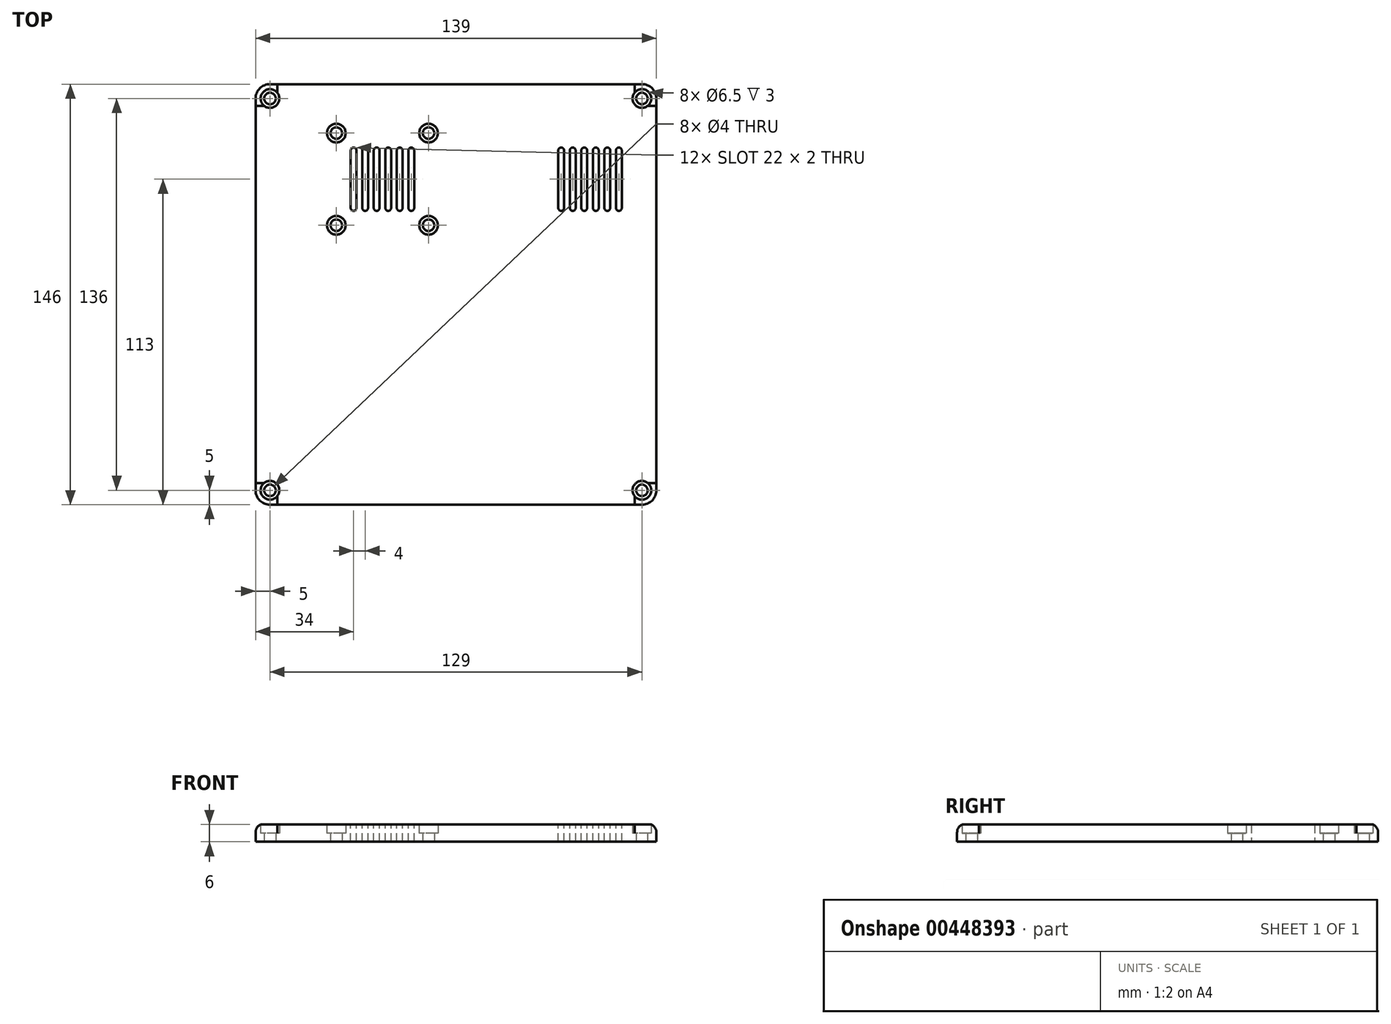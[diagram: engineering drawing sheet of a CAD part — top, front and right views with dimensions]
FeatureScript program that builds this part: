
annotation { "Feature Type Name" : "Feature", "Feature Type Description" : "" }
export const myFeature = defineFeature(function(context is Context, id is Id, definition is map)
    precondition{}
    {
        {
            var Q0;
            Q0=qCreatedBy(makeId("Top.planeOp"),FACE);
            var sketch = newSketch(context, id + "F0", { "sketchPlane" : qUnion([Q0])});
            skLineSegment(sketch, "E0.bottom", {"start": v(63.5, -70) * mm, "end": v(-63.5, -70) * mm});
            skLineSegment(sketch, "E0.top", {"start": v(63.5, 70) * mm, "end": v(-63.5, 70) * mm});
            skLineSegment(sketch, "E0.left", {"start": v(66.5, -67) * mm, "end": v(66.5, 67) * mm});
            skLineSegment(sketch, "E0.right", {"start": v(-66.5, -67) * mm, "end": v(-66.5, 67) * mm});
            skPoint(sketch, "E0.middle", {"position": v(0, 0) * mm});
            skLineSegment(sketch, "E1.bottom", {"start": v(64.5, -73) * mm, "end": v(-64.5, -73) * mm});
            skLineSegment(sketch, "E1.top", {"start": v(64.5, 73) * mm, "end": v(-64.5, 73) * mm});
            skLineSegment(sketch, "E1.left", {"start": v(69.5, -68) * mm, "end": v(69.5, 68) * mm});
            skLineSegment(sketch, "E1.right", {"start": v(-69.5, -68) * mm, "end": v(-69.5, 68) * mm});
            skPoint(sketch, "E2.visualSharp", {"position": v(-69.5, 73) * mm});
            skArc(sketch, "E2.filletArc", {"start": v(-64.5, 73) * mm, "mid": v(-68.04, 71.54) * mm, "end": v(-69.5, 68) * mm});
            skPoint(sketch, "E3.visualSharp", {"position": v(69.5, 73) * mm});
            skArc(sketch, "E3.filletArc", {"start": v(69.5, 68) * mm, "mid": v(68.04, 71.54) * mm, "end": v(64.5, 73) * mm});
            skPoint(sketch, "E4.visualSharp", {"position": v(-69.5, -73) * mm});
            skArc(sketch, "E4.filletArc", {"start": v(-69.5, -68) * mm, "mid": v(-68.04, -71.54) * mm, "end": v(-64.5, -73) * mm});
            skPoint(sketch, "E5.visualSharp", {"position": v(69.5, -73) * mm});
            skArc(sketch, "E5.filletArc", {"start": v(64.5, -73) * mm, "mid": v(68.04, -71.54) * mm, "end": v(69.5, -68) * mm});
            skPoint(sketch, "E6.visualSharp", {"position": v(66.5, 70) * mm});
            skArc(sketch, "E6.filletArc", {"start": v(66.5, 67) * mm, "mid": v(65.62, 69.12) * mm, "end": v(63.5, 70) * mm});
            skPoint(sketch, "E7.visualSharp", {"position": v(-66.5, 70) * mm});
            skArc(sketch, "E7.filletArc", {"start": v(-63.5, 70) * mm, "mid": v(-65.62, 69.12) * mm, "end": v(-66.5, 67) * mm});
            skPoint(sketch, "E8.visualSharp", {"position": v(-66.5, -70) * mm});
            skArc(sketch, "E8.filletArc", {"start": v(-66.5, -67) * mm, "mid": v(-65.62, -69.12) * mm, "end": v(-63.5, -70) * mm});
            skPoint(sketch, "E9.visualSharp", {"position": v(66.5, -70) * mm});
            skArc(sketch, "E9.filletArc", {"start": v(63.5, -70) * mm, "mid": v(65.62, -69.12) * mm, "end": v(66.5, -67) * mm});
            skCircle(sketch, "E10", {"center": v(-64.5, 68) * mm, "radius": 3.25 * mm});
            skCircle(sketch, "E11", {"center": v(-64.5, 68) * mm, "radius": 2 * mm});
            skCircle(sketch, "E12", {"center": v(64.5, 68) * mm, "radius": 3.25 * mm});
            skCircle(sketch, "E13", {"center": v(64.5, 68) * mm, "radius": 2 * mm});
            skCircle(sketch, "E14", {"center": v(64.5, -68) * mm, "radius": 3.25 * mm});
            skCircle(sketch, "E15", {"center": v(64.5, -68) * mm, "radius": 2 * mm});
            skCircle(sketch, "E16", {"center": v(-64.5, -68) * mm, "radius": 3.25 * mm});
            skCircle(sketch, "E17", {"center": v(-64.5, -68) * mm, "radius": 2 * mm});
            skCircle(sketch, "E18", {"center": v(-41.5, 56) * mm, "radius": 3.25 * mm});
            skCircle(sketch, "E19", {"center": v(-9.5, 56) * mm, "radius": 3.25 * mm});
            skCircle(sketch, "E20", {"center": v(-41.5, 24) * mm, "radius": 3.25 * mm});
            skCircle(sketch, "E21", {"center": v(-9.5, 24) * mm, "radius": 3.25 * mm});
            skCircle(sketch, "E22", {"center": v(-9.5, 56) * mm, "radius": 2 * mm});
            skCircle(sketch, "E23", {"center": v(-41.5, 56) * mm, "radius": 2 * mm});
            skCircle(sketch, "E24", {"center": v(-41.5, 24) * mm, "radius": 2 * mm});
            skCircle(sketch, "E25", {"center": v(-9.5, 24) * mm, "radius": 2 * mm});
            skSolve(sketch);
        }
        {
            var Q0;
            {var subQ5=sQuery(id+"F0.wireOp",EDGE,"E14");var subQ10=sQuery(id+"F0.wireOp",EDGE,"E0.bottom");var subQ11=makeQuery(id+"F0.imprint","INTERSECT",VERTEX,{"derivedFrom":[subQ10,subQ5]});Q0=makeQuery(id+"F0.imprint","IMPRINT",FACE,{"disambiguationData":[TD([[makeQuery(id+"F0.imprint","IMPRINT",EDGE,{"disambiguationData":[TD([[subQ11,-1.0]])],"derivedFrom":subQ10}),-1.0]])]});}
            var Q1;
            Q1=makeQuery(id+"F0.imprint","IMPRINT",FACE,{"disambiguationData":[TD([[makeQuery(id+"F0.imprint","IMPRINT",EDGE,{"derivedFrom":sQuery(id+"F0.wireOp",EDGE,"E1.bottom")}),-1.0]])]});
            extrude(context, id + "F1", {"entities" : qUnion([Q0, Q1]), "depth" : 6 * mm});
        }
        {
            var Q0;
            Q0 = qSketchRegion(id + "F0", true);
            var Q1;
            {var subQ0=sQuery(id+"F0.wireOp",EDGE,"E7.filletArc");var subQ1=sQuery(id+"F0.wireOp",EDGE,"E0.top");var subQ2=makeQuery(id+"F0.imprint","INTERSECT",VERTEX,{"derivedFrom":[subQ1,subQ0]});Q1=makeQuery(id+"F0.imprint","IMPRINT",FACE,{"disambiguationData":[TD([[makeQuery(id+"F0.imprint","IMPRINT",EDGE,{"disambiguationData":[TD([[subQ2,1.0]])],"derivedFrom":subQ1}),1.0]])]});}
            var Q2;
            {var subQ0=sQuery(id+"F0.wireOp",EDGE,"E7.filletArc");var subQ1=sQuery(id+"F0.wireOp",EDGE,"E0.top");var subQ2=makeQuery(id+"F0.imprint","INTERSECT",VERTEX,{"derivedFrom":[subQ1,subQ0]});Q2=makeQuery(id+"F0.imprint","IMPRINT",FACE,{"disambiguationData":[TD([[makeQuery(id+"F0.imprint","IMPRINT",EDGE,{"disambiguationData":[TD([[subQ2,1.0]])],"derivedFrom":subQ1}),-1.0]])]});}
            var Q3;
            {var subQ0=sQuery(id+"F0.wireOp",EDGE,"E8.filletArc");var subQ1=sQuery(id+"F0.wireOp",EDGE,"E0.bottom");var subQ2=makeQuery(id+"F0.imprint","INTERSECT",VERTEX,{"derivedFrom":[subQ1,subQ0]});Q3=makeQuery(id+"F0.imprint","IMPRINT",FACE,{"disambiguationData":[TD([[makeQuery(id+"F0.imprint","IMPRINT",EDGE,{"disambiguationData":[TD([[subQ2,1.0]])],"derivedFrom":subQ1}),-1.0]])]});}
            var Q4;
            {var subQ0=sQuery(id+"F0.wireOp",EDGE,"E8.filletArc");var subQ1=sQuery(id+"F0.wireOp",EDGE,"E0.bottom");var subQ2=makeQuery(id+"F0.imprint","INTERSECT",VERTEX,{"derivedFrom":[subQ1,subQ0]});Q4=makeQuery(id+"F0.imprint","IMPRINT",FACE,{"disambiguationData":[TD([[makeQuery(id+"F0.imprint","IMPRINT",EDGE,{"disambiguationData":[TD([[subQ2,1.0]])],"derivedFrom":subQ1}),1.0]])]});}
            var Q5;
            {var subQ0=sQuery(id+"F0.wireOp",EDGE,"E9.filletArc");var subQ1=sQuery(id+"F0.wireOp",EDGE,"E0.bottom");var subQ2=makeQuery(id+"F0.imprint","INTERSECT",VERTEX,{"derivedFrom":[subQ1,subQ0]});Q5=makeQuery(id+"F0.imprint","IMPRINT",FACE,{"disambiguationData":[TD([[makeQuery(id+"F0.imprint","IMPRINT",EDGE,{"disambiguationData":[TD([[subQ2,-1.0]])],"derivedFrom":subQ1}),-1.0]])]});}
            var Q6;
            {var subQ0=sQuery(id+"F0.wireOp",EDGE,"E9.filletArc");var subQ1=sQuery(id+"F0.wireOp",EDGE,"E0.bottom");var subQ2=makeQuery(id+"F0.imprint","INTERSECT",VERTEX,{"derivedFrom":[subQ1,subQ0]});Q6=makeQuery(id+"F0.imprint","IMPRINT",FACE,{"disambiguationData":[TD([[makeQuery(id+"F0.imprint","IMPRINT",EDGE,{"disambiguationData":[TD([[subQ2,-1.0]])],"derivedFrom":subQ1}),1.0]])]});}
            var Q7;
            {var subQ0=sQuery(id+"F0.wireOp",EDGE,"E6.filletArc");var subQ1=sQuery(id+"F0.wireOp",EDGE,"E0.top");var subQ2=makeQuery(id+"F0.imprint","INTERSECT",VERTEX,{"derivedFrom":[subQ1,subQ0]});Q7=makeQuery(id+"F0.imprint","IMPRINT",FACE,{"disambiguationData":[TD([[makeQuery(id+"F0.imprint","IMPRINT",EDGE,{"disambiguationData":[TD([[subQ2,-1.0]])],"derivedFrom":subQ1}),-1.0]])]});}
            var Q8;
            {var subQ0=sQuery(id+"F0.wireOp",EDGE,"E6.filletArc");var subQ1=sQuery(id+"F0.wireOp",EDGE,"E0.top");var subQ2=makeQuery(id+"F0.imprint","INTERSECT",VERTEX,{"derivedFrom":[subQ1,subQ0]});Q8=makeQuery(id+"F0.imprint","IMPRINT",FACE,{"disambiguationData":[TD([[makeQuery(id+"F0.imprint","IMPRINT",EDGE,{"disambiguationData":[TD([[subQ2,-1.0]])],"derivedFrom":subQ1}),1.0]])]});}
            var Q9;
            Q9=makeQuery(id+"F0.imprint","IMPRINT",FACE,{"disambiguationData":[TD([[makeQuery(id+"F0.imprint","IMPRINT",EDGE,{"derivedFrom":sQuery(id+"F0.wireOp",EDGE,"E18")}),1.0]])]});
            var Q10;
            Q10=makeQuery(id+"F0.imprint","IMPRINT",FACE,{"disambiguationData":[TD([[makeQuery(id+"F0.imprint","IMPRINT",EDGE,{"derivedFrom":sQuery(id+"F0.wireOp",EDGE,"E19")}),1.0]])]});
            var Q11;
            Q11=makeQuery(id+"F0.imprint","IMPRINT",FACE,{"disambiguationData":[TD([[makeQuery(id+"F0.imprint","IMPRINT",EDGE,{"derivedFrom":sQuery(id+"F0.wireOp",EDGE,"E20")}),1.0]])]});
            var Q12;
            Q12=makeQuery(id+"F0.imprint","IMPRINT",FACE,{"disambiguationData":[TD([[makeQuery(id+"F0.imprint","IMPRINT",EDGE,{"derivedFrom":sQuery(id+"F0.wireOp",EDGE,"E21")}),1.0]])]});
            extrude(context, id + "F2", {"entities" : qUnion([Q0, Q1, Q2, Q3, Q4, Q5, Q6, Q7, Q8, Q9, Q10, Q11, Q12]), "operationType" : NewBodyOperationType.ADD, "depth" : 3 * mm});
        }
        {
            var Q0;
            Q0=makeQuery(id+"F1.opExtrude","CAP_EDGE",EDGE,{"disambiguationData":[OSD([sQuery(id+"F0.wireOp",EDGE,"E1.bottom")])],"isStart":false});
            fillet(context, id + "F3", {"entities" : qUnion([Q0]), "radius" : 3 * mm, "tangentPropagation" : true, "allowEdgeOverflow" : false});
        }
        {
            var Q0;
            Q0=makeQuery(id+"F1.opExtrude","CAP_FACE",FACE,{"disambiguationData":[OSD([sQuery(id+"F0.wireOp",EDGE,"E1.bottom"),sQuery(id+"F0.wireOp",EDGE,"E1.top"),sQuery(id+"F0.wireOp",EDGE,"E1.left"),sQuery(id+"F0.wireOp",EDGE,"E1.right"),sQuery(id+"F0.wireOp",EDGE,"E2.filletArc"),sQuery(id+"F0.wireOp",EDGE,"E3.filletArc"),sQuery(id+"F0.wireOp",EDGE,"E4.filletArc"),sQuery(id+"F0.wireOp",EDGE,"E5.filletArc"),sQuery(id+"F0.wireOp",EDGE,"E10"),sQuery(id+"F0.wireOp",EDGE,"E12"),sQuery(id+"F0.wireOp",EDGE,"E14"),sQuery(id+"F0.wireOp",EDGE,"E16"),sQuery(id+"F0.wireOp",EDGE,"E18"),sQuery(id+"F0.wireOp",EDGE,"E19"),sQuery(id+"F0.wireOp",EDGE,"E20"),sQuery(id+"F0.wireOp",EDGE,"E21")])],"isStart":false});
            var sketch = newSketch(context, id + "F4", { "sketchPlane" : qUnion([Q0])});
            skLineSegment(sketch, "E26.bottom", {"start": v(-30.5, 29) * mm, "end": v(-32.5, 29) * mm});
            skLineSegment(sketch, "E26.top", {"start": v(-30.5, 51) * mm, "end": v(-32.5, 51) * mm});
            skLineSegment(sketch, "E26.left", {"start": v(-30.5, 29) * mm, "end": v(-30.5, 51) * mm});
            skLineSegment(sketch, "E26.right", {"start": v(-32.5, 29) * mm, "end": v(-32.5, 51) * mm});
            skPoint(sketch, "E26.middle", {"position": v(-31.5, 40) * mm});
            skLineSegment(sketch, "E27.bottom", {"start": v(-26.5, 29) * mm, "end": v(-28.5, 29) * mm});
            skLineSegment(sketch, "E27.top", {"start": v(-26.5, 51) * mm, "end": v(-28.5, 51) * mm});
            skLineSegment(sketch, "E27.left", {"start": v(-26.5, 29) * mm, "end": v(-26.5, 51) * mm});
            skLineSegment(sketch, "E27.right", {"start": v(-28.5, 29) * mm, "end": v(-28.5, 51) * mm});
            skPoint(sketch, "E27.middle", {"position": v(-27.5, 40) * mm});
            skLineSegment(sketch, "E28.bottom", {"start": v(-22.5, 29) * mm, "end": v(-24.5, 29) * mm});
            skLineSegment(sketch, "E28.top", {"start": v(-22.5, 51) * mm, "end": v(-24.5, 51) * mm});
            skLineSegment(sketch, "E28.left", {"start": v(-22.5, 29) * mm, "end": v(-22.5, 51) * mm});
            skLineSegment(sketch, "E28.right", {"start": v(-24.5, 29) * mm, "end": v(-24.5, 51) * mm});
            skPoint(sketch, "E28.middle", {"position": v(-23.5, 40) * mm});
            skLineSegment(sketch, "E29.bottom", {"start": v(-18.5, 29) * mm, "end": v(-20.5, 29) * mm});
            skLineSegment(sketch, "E29.top", {"start": v(-18.5, 51) * mm, "end": v(-20.5, 51) * mm});
            skLineSegment(sketch, "E29.left", {"start": v(-18.5, 29) * mm, "end": v(-18.5, 51) * mm});
            skLineSegment(sketch, "E29.right", {"start": v(-20.5, 29) * mm, "end": v(-20.5, 51) * mm});
            skPoint(sketch, "E29.middle", {"position": v(-19.5, 40) * mm});
            skLineSegment(sketch, "E30.bottom", {"start": v(-14.5, 29) * mm, "end": v(-16.5, 29) * mm});
            skLineSegment(sketch, "E30.top", {"start": v(-14.5, 51) * mm, "end": v(-16.5, 51) * mm});
            skLineSegment(sketch, "E30.left", {"start": v(-14.5, 29) * mm, "end": v(-14.5, 51) * mm});
            skLineSegment(sketch, "E30.right", {"start": v(-16.5, 29) * mm, "end": v(-16.5, 51) * mm});
            skPoint(sketch, "E30.middle", {"position": v(-15.5, 40) * mm});
            skLineSegment(sketch, "E31.bottom", {"start": v(-34.5, 29) * mm, "end": v(-36.5, 29) * mm});
            skLineSegment(sketch, "E31.top", {"start": v(-34.5, 51) * mm, "end": v(-36.5, 51) * mm});
            skLineSegment(sketch, "E31.left", {"start": v(-34.5, 29) * mm, "end": v(-34.5, 51) * mm});
            skLineSegment(sketch, "E31.right", {"start": v(-36.5, 29) * mm, "end": v(-36.5, 51) * mm});
            skPoint(sketch, "E31.middle", {"position": v(-35.5, 40) * mm});
            skLineSegment(sketch, "E32.bottom", {"start": v(41.5, 29) * mm, "end": v(39.5, 29) * mm});
            skLineSegment(sketch, "E32.top", {"start": v(41.5, 51) * mm, "end": v(39.5, 51) * mm});
            skLineSegment(sketch, "E32.left", {"start": v(41.5, 29) * mm, "end": v(41.5, 51) * mm});
            skLineSegment(sketch, "E32.right", {"start": v(39.5, 29) * mm, "end": v(39.5, 51) * mm});
            skPoint(sketch, "E32.middle", {"position": v(40.5, 40) * mm});
            skLineSegment(sketch, "E33.bottom", {"start": v(45.5, 29) * mm, "end": v(43.5, 29) * mm});
            skLineSegment(sketch, "E33.top", {"start": v(45.5, 51) * mm, "end": v(43.5, 51) * mm});
            skLineSegment(sketch, "E33.left", {"start": v(45.5, 29) * mm, "end": v(45.5, 51) * mm});
            skLineSegment(sketch, "E33.right", {"start": v(43.5, 29) * mm, "end": v(43.5, 51) * mm});
            skPoint(sketch, "E33.middle", {"position": v(44.5, 40) * mm});
            skLineSegment(sketch, "E34.bottom", {"start": v(49.5, 29) * mm, "end": v(47.5, 29) * mm});
            skLineSegment(sketch, "E34.top", {"start": v(49.5, 51) * mm, "end": v(47.5, 51) * mm});
            skLineSegment(sketch, "E34.left", {"start": v(49.5, 29) * mm, "end": v(49.5, 51) * mm});
            skLineSegment(sketch, "E34.right", {"start": v(47.5, 29) * mm, "end": v(47.5, 51) * mm});
            skPoint(sketch, "E34.middle", {"position": v(48.5, 40) * mm});
            skLineSegment(sketch, "E35.bottom", {"start": v(53.5, 29) * mm, "end": v(51.5, 29) * mm});
            skLineSegment(sketch, "E35.top", {"start": v(53.5, 51) * mm, "end": v(51.5, 51) * mm});
            skLineSegment(sketch, "E35.left", {"start": v(53.5, 29) * mm, "end": v(53.5, 51) * mm});
            skLineSegment(sketch, "E35.right", {"start": v(51.5, 29) * mm, "end": v(51.5, 51) * mm});
            skPoint(sketch, "E35.middle", {"position": v(52.5, 40) * mm});
            skLineSegment(sketch, "E36.bottom", {"start": v(57.5, 29) * mm, "end": v(55.5, 29) * mm});
            skLineSegment(sketch, "E36.top", {"start": v(57.5, 51) * mm, "end": v(55.5, 51) * mm});
            skLineSegment(sketch, "E36.left", {"start": v(57.5, 29) * mm, "end": v(57.5, 51) * mm});
            skLineSegment(sketch, "E36.right", {"start": v(55.5, 29) * mm, "end": v(55.5, 51) * mm});
            skPoint(sketch, "E36.middle", {"position": v(56.5, 40) * mm});
            skLineSegment(sketch, "E37.bottom", {"start": v(37.5, 29) * mm, "end": v(35.5, 29) * mm});
            skLineSegment(sketch, "E37.top", {"start": v(37.5, 51) * mm, "end": v(35.5, 51) * mm});
            skLineSegment(sketch, "E37.left", {"start": v(37.5, 29) * mm, "end": v(37.5, 51) * mm});
            skLineSegment(sketch, "E37.right", {"start": v(35.5, 29) * mm, "end": v(35.5, 51) * mm});
            skPoint(sketch, "E37.middle", {"position": v(36.5, 40) * mm});
            skSolve(sketch);
        }
        {
            var Q0;
            Q0=makeQuery(id+"F4.imprint","IMPRINT",FACE,{"disambiguationData":[TD([[makeQuery(id+"F4.imprint","IMPRINT",EDGE,{"derivedFrom":sQuery(id+"F4.wireOp",EDGE,"E31.bottom")}),-1.0]])]});
            var Q1;
            Q1=makeQuery(id+"F4.imprint","IMPRINT",FACE,{"disambiguationData":[TD([[makeQuery(id+"F4.imprint","IMPRINT",EDGE,{"derivedFrom":sQuery(id+"F4.wireOp",EDGE,"E26.bottom")}),-1.0]])]});
            var Q2;
            Q2=makeQuery(id+"F4.imprint","IMPRINT",FACE,{"disambiguationData":[TD([[makeQuery(id+"F4.imprint","IMPRINT",EDGE,{"derivedFrom":sQuery(id+"F4.wireOp",EDGE,"E27.bottom")}),-1.0]])]});
            var Q3;
            Q3=makeQuery(id+"F4.imprint","IMPRINT",FACE,{"disambiguationData":[TD([[makeQuery(id+"F4.imprint","IMPRINT",EDGE,{"derivedFrom":sQuery(id+"F4.wireOp",EDGE,"E28.bottom")}),-1.0]])]});
            var Q4;
            Q4=makeQuery(id+"F4.imprint","IMPRINT",FACE,{"disambiguationData":[TD([[makeQuery(id+"F4.imprint","IMPRINT",EDGE,{"derivedFrom":sQuery(id+"F4.wireOp",EDGE,"E29.bottom")}),-1.0]])]});
            var Q5;
            Q5=makeQuery(id+"F4.imprint","IMPRINT",FACE,{"disambiguationData":[TD([[makeQuery(id+"F4.imprint","IMPRINT",EDGE,{"derivedFrom":sQuery(id+"F4.wireOp",EDGE,"E30.bottom")}),-1.0]])]});
            var Q6;
            Q6=makeQuery(id+"F4.imprint","IMPRINT",FACE,{"disambiguationData":[TD([[makeQuery(id+"F4.imprint","IMPRINT",EDGE,{"derivedFrom":sQuery(id+"F4.wireOp",EDGE,"E37.bottom")}),-1.0]])]});
            var Q7;
            Q7=makeQuery(id+"F4.imprint","IMPRINT",FACE,{"disambiguationData":[TD([[makeQuery(id+"F4.imprint","IMPRINT",EDGE,{"derivedFrom":sQuery(id+"F4.wireOp",EDGE,"E32.bottom")}),-1.0]])]});
            var Q8;
            Q8=makeQuery(id+"F4.imprint","IMPRINT",FACE,{"disambiguationData":[TD([[makeQuery(id+"F4.imprint","IMPRINT",EDGE,{"derivedFrom":sQuery(id+"F4.wireOp",EDGE,"E33.bottom")}),-1.0]])]});
            var Q9;
            Q9=makeQuery(id+"F4.imprint","IMPRINT",FACE,{"disambiguationData":[TD([[makeQuery(id+"F4.imprint","IMPRINT",EDGE,{"derivedFrom":sQuery(id+"F4.wireOp",EDGE,"E34.bottom")}),-1.0]])]});
            var Q10;
            Q10=makeQuery(id+"F4.imprint","IMPRINT",FACE,{"disambiguationData":[TD([[makeQuery(id+"F4.imprint","IMPRINT",EDGE,{"derivedFrom":sQuery(id+"F4.wireOp",EDGE,"E35.bottom")}),-1.0]])]});
            var Q11;
            Q11=makeQuery(id+"F4.imprint","IMPRINT",FACE,{"disambiguationData":[TD([[makeQuery(id+"F4.imprint","IMPRINT",EDGE,{"derivedFrom":sQuery(id+"F4.wireOp",EDGE,"E36.bottom")}),-1.0]])]});
            extrude(context, id + "F5", {"entities" : qUnion([Q0, Q1, Q2, Q3, Q4, Q5, Q6, Q7, Q8, Q9, Q10, Q11]), "operationType" : NewBodyOperationType.REMOVE, "oppositeDirection" : true, "depth" : 6 * mm});
        }
        {
            var Q0;
            Q0=makeQuery(id+"F5.boolean.opBoolean","COPY",EDGE,{"derivedFrom":makeQuery(id+"F5.opExtrude","SWEPT_EDGE",EDGE,{"disambiguationData":[OSD([sQuery(id+"F4.wireOp",EDGE,"E31.top"),sQuery(id+"F4.wireOp",EDGE,"E31.right")])]})});
            var Q1;
            Q1=makeQuery(id+"F5.boolean.opBoolean","COPY",EDGE,{"derivedFrom":makeQuery(id+"F5.opExtrude","SWEPT_EDGE",EDGE,{"disambiguationData":[OSD([sQuery(id+"F4.wireOp",EDGE,"E26.top"),sQuery(id+"F4.wireOp",EDGE,"E26.right")])]})});
            var Q2;
            Q2=makeQuery(id+"F5.boolean.opBoolean","COPY",EDGE,{"derivedFrom":makeQuery(id+"F5.opExtrude","SWEPT_EDGE",EDGE,{"disambiguationData":[OSD([sQuery(id+"F4.wireOp",EDGE,"E27.top"),sQuery(id+"F4.wireOp",EDGE,"E27.right")])]})});
            var Q3;
            Q3=makeQuery(id+"F5.boolean.opBoolean","COPY",EDGE,{"derivedFrom":makeQuery(id+"F5.opExtrude","SWEPT_EDGE",EDGE,{"disambiguationData":[OSD([sQuery(id+"F4.wireOp",EDGE,"E28.top"),sQuery(id+"F4.wireOp",EDGE,"E28.right")])]})});
            var Q4;
            Q4=makeQuery(id+"F5.boolean.opBoolean","COPY",EDGE,{"derivedFrom":makeQuery(id+"F5.opExtrude","SWEPT_EDGE",EDGE,{"disambiguationData":[OSD([sQuery(id+"F4.wireOp",EDGE,"E29.top"),sQuery(id+"F4.wireOp",EDGE,"E29.right")])]})});
            var Q5;
            Q5=makeQuery(id+"F5.boolean.opBoolean","COPY",EDGE,{"derivedFrom":makeQuery(id+"F5.opExtrude","SWEPT_EDGE",EDGE,{"disambiguationData":[OSD([sQuery(id+"F4.wireOp",EDGE,"E30.top"),sQuery(id+"F4.wireOp",EDGE,"E30.right")])]})});
            var Q6;
            Q6=makeQuery(id+"F5.boolean.opBoolean","COPY",EDGE,{"derivedFrom":makeQuery(id+"F5.opExtrude","SWEPT_EDGE",EDGE,{"disambiguationData":[OSD([sQuery(id+"F4.wireOp",EDGE,"E30.top"),sQuery(id+"F4.wireOp",EDGE,"E30.left")])]})});
            var Q7;
            Q7=makeQuery(id+"F5.boolean.opBoolean","COPY",EDGE,{"derivedFrom":makeQuery(id+"F5.opExtrude","SWEPT_EDGE",EDGE,{"disambiguationData":[OSD([sQuery(id+"F4.wireOp",EDGE,"E29.top"),sQuery(id+"F4.wireOp",EDGE,"E29.left")])]})});
            var Q8;
            Q8=makeQuery(id+"F5.boolean.opBoolean","COPY",EDGE,{"derivedFrom":makeQuery(id+"F5.opExtrude","SWEPT_EDGE",EDGE,{"disambiguationData":[OSD([sQuery(id+"F4.wireOp",EDGE,"E28.top"),sQuery(id+"F4.wireOp",EDGE,"E28.left")])]})});
            var Q9;
            Q9=makeQuery(id+"F5.boolean.opBoolean","COPY",EDGE,{"derivedFrom":makeQuery(id+"F5.opExtrude","SWEPT_EDGE",EDGE,{"disambiguationData":[OSD([sQuery(id+"F4.wireOp",EDGE,"E26.top"),sQuery(id+"F4.wireOp",EDGE,"E26.left")])]})});
            var Q10;
            Q10=makeQuery(id+"F5.boolean.opBoolean","COPY",EDGE,{"derivedFrom":makeQuery(id+"F5.opExtrude","SWEPT_EDGE",EDGE,{"disambiguationData":[OSD([sQuery(id+"F4.wireOp",EDGE,"E31.top"),sQuery(id+"F4.wireOp",EDGE,"E31.left")])]})});
            var Q11;
            Q11=makeQuery(id+"F5.boolean.opBoolean","COPY",EDGE,{"derivedFrom":makeQuery(id+"F5.opExtrude","SWEPT_EDGE",EDGE,{"disambiguationData":[OSD([sQuery(id+"F4.wireOp",EDGE,"E27.top"),sQuery(id+"F4.wireOp",EDGE,"E27.left")])]})});
            var Q12;
            Q12=makeQuery(id+"F5.boolean.opBoolean","COPY",EDGE,{"derivedFrom":makeQuery(id+"F5.opExtrude","SWEPT_EDGE",EDGE,{"disambiguationData":[OSD([sQuery(id+"F4.wireOp",EDGE,"E30.bottom"),sQuery(id+"F4.wireOp",EDGE,"E30.left")])]})});
            var Q13;
            Q13=makeQuery(id+"F5.boolean.opBoolean","COPY",EDGE,{"derivedFrom":makeQuery(id+"F5.opExtrude","SWEPT_EDGE",EDGE,{"disambiguationData":[OSD([sQuery(id+"F4.wireOp",EDGE,"E29.bottom"),sQuery(id+"F4.wireOp",EDGE,"E29.left")])]})});
            var Q14;
            Q14=makeQuery(id+"F5.boolean.opBoolean","COPY",EDGE,{"derivedFrom":makeQuery(id+"F5.opExtrude","SWEPT_EDGE",EDGE,{"disambiguationData":[OSD([sQuery(id+"F4.wireOp",EDGE,"E28.bottom"),sQuery(id+"F4.wireOp",EDGE,"E28.left")])]})});
            var Q15;
            Q15=makeQuery(id+"F5.boolean.opBoolean","COPY",EDGE,{"derivedFrom":makeQuery(id+"F5.opExtrude","SWEPT_EDGE",EDGE,{"disambiguationData":[OSD([sQuery(id+"F4.wireOp",EDGE,"E27.bottom"),sQuery(id+"F4.wireOp",EDGE,"E27.left")])]})});
            var Q16;
            Q16=makeQuery(id+"F5.boolean.opBoolean","COPY",EDGE,{"derivedFrom":makeQuery(id+"F5.opExtrude","SWEPT_EDGE",EDGE,{"disambiguationData":[OSD([sQuery(id+"F4.wireOp",EDGE,"E26.bottom"),sQuery(id+"F4.wireOp",EDGE,"E26.left")])]})});
            var Q17;
            Q17=makeQuery(id+"F5.boolean.opBoolean","COPY",EDGE,{"derivedFrom":makeQuery(id+"F5.opExtrude","SWEPT_EDGE",EDGE,{"disambiguationData":[OSD([sQuery(id+"F4.wireOp",EDGE,"E31.bottom"),sQuery(id+"F4.wireOp",EDGE,"E31.left")])]})});
            var Q18;
            Q18=makeQuery(id+"F5.boolean.opBoolean","COPY",EDGE,{"derivedFrom":makeQuery(id+"F5.opExtrude","SWEPT_EDGE",EDGE,{"disambiguationData":[OSD([sQuery(id+"F4.wireOp",EDGE,"E30.bottom"),sQuery(id+"F4.wireOp",EDGE,"E30.right")])]})});
            var Q19;
            Q19=makeQuery(id+"F5.boolean.opBoolean","COPY",EDGE,{"derivedFrom":makeQuery(id+"F5.opExtrude","SWEPT_EDGE",EDGE,{"disambiguationData":[OSD([sQuery(id+"F4.wireOp",EDGE,"E29.bottom"),sQuery(id+"F4.wireOp",EDGE,"E29.right")])]})});
            var Q20;
            Q20=makeQuery(id+"F5.boolean.opBoolean","COPY",EDGE,{"derivedFrom":makeQuery(id+"F5.opExtrude","SWEPT_EDGE",EDGE,{"disambiguationData":[OSD([sQuery(id+"F4.wireOp",EDGE,"E28.bottom"),sQuery(id+"F4.wireOp",EDGE,"E28.right")])]})});
            var Q21;
            Q21=makeQuery(id+"F5.boolean.opBoolean","COPY",EDGE,{"derivedFrom":makeQuery(id+"F5.opExtrude","SWEPT_EDGE",EDGE,{"disambiguationData":[OSD([sQuery(id+"F4.wireOp",EDGE,"E27.bottom"),sQuery(id+"F4.wireOp",EDGE,"E27.right")])]})});
            var Q22;
            Q22=makeQuery(id+"F5.boolean.opBoolean","COPY",EDGE,{"derivedFrom":makeQuery(id+"F5.opExtrude","SWEPT_EDGE",EDGE,{"disambiguationData":[OSD([sQuery(id+"F4.wireOp",EDGE,"E26.bottom"),sQuery(id+"F4.wireOp",EDGE,"E26.right")])]})});
            var Q23;
            Q23=makeQuery(id+"F5.boolean.opBoolean","COPY",EDGE,{"derivedFrom":makeQuery(id+"F5.opExtrude","SWEPT_EDGE",EDGE,{"disambiguationData":[OSD([sQuery(id+"F4.wireOp",EDGE,"E31.bottom"),sQuery(id+"F4.wireOp",EDGE,"E31.right")])]})});
            var Q24;
            Q24=makeQuery(id+"F5.boolean.opBoolean","COPY",EDGE,{"derivedFrom":makeQuery(id+"F5.opExtrude","CAP_EDGE",EDGE,{"disambiguationData":[OSD([sQuery(id+"F4.wireOp",EDGE,"E30.left")])],"isStart":true})});
            var Q25;
            Q25=makeQuery(id+"F5.boolean.opBoolean","COPY",EDGE,{"derivedFrom":makeQuery(id+"F5.opExtrude","CAP_EDGE",EDGE,{"disambiguationData":[OSD([sQuery(id+"F4.wireOp",EDGE,"E29.left")])],"isStart":true})});
            var Q26;
            Q26=makeQuery(id+"F5.boolean.opBoolean","COPY",EDGE,{"derivedFrom":makeQuery(id+"F5.opExtrude","CAP_EDGE",EDGE,{"disambiguationData":[OSD([sQuery(id+"F4.wireOp",EDGE,"E28.left")])],"isStart":true})});
            var Q27;
            Q27=makeQuery(id+"F5.boolean.opBoolean","COPY",EDGE,{"derivedFrom":makeQuery(id+"F5.opExtrude","CAP_EDGE",EDGE,{"disambiguationData":[OSD([sQuery(id+"F4.wireOp",EDGE,"E27.left")])],"isStart":true})});
            var Q28;
            Q28=makeQuery(id+"F5.boolean.opBoolean","COPY",EDGE,{"derivedFrom":makeQuery(id+"F5.opExtrude","CAP_EDGE",EDGE,{"disambiguationData":[OSD([sQuery(id+"F4.wireOp",EDGE,"E26.left")])],"isStart":true})});
            var Q29;
            Q29=makeQuery(id+"F5.boolean.opBoolean","COPY",EDGE,{"derivedFrom":makeQuery(id+"F5.opExtrude","CAP_EDGE",EDGE,{"disambiguationData":[OSD([sQuery(id+"F4.wireOp",EDGE,"E31.left")])],"isStart":true})});
            var Q30;
            Q30=makeQuery(id+"F5.boolean.opBoolean","COPY",EDGE,{"derivedFrom":makeQuery(id+"F5.opExtrude","SWEPT_EDGE",EDGE,{"disambiguationData":[OSD([sQuery(id+"F4.wireOp",EDGE,"E37.top"),sQuery(id+"F4.wireOp",EDGE,"E37.left")])]})});
            var Q31;
            Q31=makeQuery(id+"F5.boolean.opBoolean","COPY",EDGE,{"derivedFrom":makeQuery(id+"F5.opExtrude","SWEPT_EDGE",EDGE,{"disambiguationData":[OSD([sQuery(id+"F4.wireOp",EDGE,"E32.top"),sQuery(id+"F4.wireOp",EDGE,"E32.left")])]})});
            var Q32;
            Q32=makeQuery(id+"F5.boolean.opBoolean","COPY",EDGE,{"derivedFrom":makeQuery(id+"F5.opExtrude","SWEPT_EDGE",EDGE,{"disambiguationData":[OSD([sQuery(id+"F4.wireOp",EDGE,"E33.top"),sQuery(id+"F4.wireOp",EDGE,"E33.left")])]})});
            var Q33;
            Q33=makeQuery(id+"F5.boolean.opBoolean","COPY",EDGE,{"derivedFrom":makeQuery(id+"F5.opExtrude","SWEPT_EDGE",EDGE,{"disambiguationData":[OSD([sQuery(id+"F4.wireOp",EDGE,"E34.top"),sQuery(id+"F4.wireOp",EDGE,"E34.left")])]})});
            var Q34;
            Q34=makeQuery(id+"F5.boolean.opBoolean","COPY",EDGE,{"derivedFrom":makeQuery(id+"F5.opExtrude","SWEPT_EDGE",EDGE,{"disambiguationData":[OSD([sQuery(id+"F4.wireOp",EDGE,"E35.top"),sQuery(id+"F4.wireOp",EDGE,"E35.left")])]})});
            var Q35;
            Q35=makeQuery(id+"F5.boolean.opBoolean","COPY",EDGE,{"derivedFrom":makeQuery(id+"F5.opExtrude","SWEPT_EDGE",EDGE,{"disambiguationData":[OSD([sQuery(id+"F4.wireOp",EDGE,"E36.top"),sQuery(id+"F4.wireOp",EDGE,"E36.left")])]})});
            var Q36;
            Q36=makeQuery(id+"F5.boolean.opBoolean","COPY",EDGE,{"derivedFrom":makeQuery(id+"F5.opExtrude","SWEPT_EDGE",EDGE,{"disambiguationData":[OSD([sQuery(id+"F4.wireOp",EDGE,"E37.top"),sQuery(id+"F4.wireOp",EDGE,"E37.right")])]})});
            var Q37;
            Q37=makeQuery(id+"F5.boolean.opBoolean","COPY",EDGE,{"derivedFrom":makeQuery(id+"F5.opExtrude","SWEPT_EDGE",EDGE,{"disambiguationData":[OSD([sQuery(id+"F4.wireOp",EDGE,"E32.top"),sQuery(id+"F4.wireOp",EDGE,"E32.right")])]})});
            var Q38;
            Q38=makeQuery(id+"F5.boolean.opBoolean","COPY",EDGE,{"derivedFrom":makeQuery(id+"F5.opExtrude","SWEPT_EDGE",EDGE,{"disambiguationData":[OSD([sQuery(id+"F4.wireOp",EDGE,"E33.top"),sQuery(id+"F4.wireOp",EDGE,"E33.right")])]})});
            var Q39;
            Q39=makeQuery(id+"F5.boolean.opBoolean","COPY",EDGE,{"derivedFrom":makeQuery(id+"F5.opExtrude","SWEPT_EDGE",EDGE,{"disambiguationData":[OSD([sQuery(id+"F4.wireOp",EDGE,"E34.top"),sQuery(id+"F4.wireOp",EDGE,"E34.right")])]})});
            var Q40;
            Q40=makeQuery(id+"F5.boolean.opBoolean","COPY",EDGE,{"derivedFrom":makeQuery(id+"F5.opExtrude","SWEPT_EDGE",EDGE,{"disambiguationData":[OSD([sQuery(id+"F4.wireOp",EDGE,"E35.top"),sQuery(id+"F4.wireOp",EDGE,"E35.right")])]})});
            var Q41;
            Q41=makeQuery(id+"F5.boolean.opBoolean","COPY",EDGE,{"derivedFrom":makeQuery(id+"F5.opExtrude","SWEPT_EDGE",EDGE,{"disambiguationData":[OSD([sQuery(id+"F4.wireOp",EDGE,"E36.top"),sQuery(id+"F4.wireOp",EDGE,"E36.right")])]})});
            var Q42;
            Q42=makeQuery(id+"F5.boolean.opBoolean","COPY",EDGE,{"derivedFrom":makeQuery(id+"F5.opExtrude","SWEPT_EDGE",EDGE,{"disambiguationData":[OSD([sQuery(id+"F4.wireOp",EDGE,"E37.bottom"),sQuery(id+"F4.wireOp",EDGE,"E37.right")])]})});
            var Q43;
            Q43=makeQuery(id+"F5.boolean.opBoolean","COPY",EDGE,{"derivedFrom":makeQuery(id+"F5.opExtrude","SWEPT_EDGE",EDGE,{"disambiguationData":[OSD([sQuery(id+"F4.wireOp",EDGE,"E32.bottom"),sQuery(id+"F4.wireOp",EDGE,"E32.right")])]})});
            var Q44;
            Q44=makeQuery(id+"F5.boolean.opBoolean","COPY",EDGE,{"derivedFrom":makeQuery(id+"F5.opExtrude","SWEPT_EDGE",EDGE,{"disambiguationData":[OSD([sQuery(id+"F4.wireOp",EDGE,"E33.bottom"),sQuery(id+"F4.wireOp",EDGE,"E33.right")])]})});
            var Q45;
            Q45=makeQuery(id+"F5.boolean.opBoolean","COPY",EDGE,{"derivedFrom":makeQuery(id+"F5.opExtrude","SWEPT_EDGE",EDGE,{"disambiguationData":[OSD([sQuery(id+"F4.wireOp",EDGE,"E34.bottom"),sQuery(id+"F4.wireOp",EDGE,"E34.right")])]})});
            var Q46;
            Q46=makeQuery(id+"F5.boolean.opBoolean","COPY",EDGE,{"derivedFrom":makeQuery(id+"F5.opExtrude","SWEPT_EDGE",EDGE,{"disambiguationData":[OSD([sQuery(id+"F4.wireOp",EDGE,"E35.bottom"),sQuery(id+"F4.wireOp",EDGE,"E35.right")])]})});
            var Q47;
            Q47=makeQuery(id+"F5.boolean.opBoolean","COPY",EDGE,{"derivedFrom":makeQuery(id+"F5.opExtrude","SWEPT_EDGE",EDGE,{"disambiguationData":[OSD([sQuery(id+"F4.wireOp",EDGE,"E36.bottom"),sQuery(id+"F4.wireOp",EDGE,"E36.right")])]})});
            var Q48;
            Q48=makeQuery(id+"F5.boolean.opBoolean","COPY",EDGE,{"derivedFrom":makeQuery(id+"F5.opExtrude","SWEPT_EDGE",EDGE,{"disambiguationData":[OSD([sQuery(id+"F4.wireOp",EDGE,"E36.bottom"),sQuery(id+"F4.wireOp",EDGE,"E36.left")])]})});
            var Q49;
            Q49=makeQuery(id+"F5.boolean.opBoolean","COPY",EDGE,{"derivedFrom":makeQuery(id+"F5.opExtrude","SWEPT_EDGE",EDGE,{"disambiguationData":[OSD([sQuery(id+"F4.wireOp",EDGE,"E35.bottom"),sQuery(id+"F4.wireOp",EDGE,"E35.left")])]})});
            var Q50;
            Q50=makeQuery(id+"F5.boolean.opBoolean","COPY",EDGE,{"derivedFrom":makeQuery(id+"F5.opExtrude","SWEPT_EDGE",EDGE,{"disambiguationData":[OSD([sQuery(id+"F4.wireOp",EDGE,"E34.bottom"),sQuery(id+"F4.wireOp",EDGE,"E34.left")])]})});
            var Q51;
            Q51=makeQuery(id+"F5.boolean.opBoolean","COPY",EDGE,{"derivedFrom":makeQuery(id+"F5.opExtrude","SWEPT_EDGE",EDGE,{"disambiguationData":[OSD([sQuery(id+"F4.wireOp",EDGE,"E33.bottom"),sQuery(id+"F4.wireOp",EDGE,"E33.left")])]})});
            var Q52;
            Q52=makeQuery(id+"F5.boolean.opBoolean","COPY",EDGE,{"derivedFrom":makeQuery(id+"F5.opExtrude","SWEPT_EDGE",EDGE,{"disambiguationData":[OSD([sQuery(id+"F4.wireOp",EDGE,"E32.bottom"),sQuery(id+"F4.wireOp",EDGE,"E32.left")])]})});
            var Q53;
            Q53=makeQuery(id+"F5.boolean.opBoolean","COPY",EDGE,{"derivedFrom":makeQuery(id+"F5.opExtrude","SWEPT_EDGE",EDGE,{"disambiguationData":[OSD([sQuery(id+"F4.wireOp",EDGE,"E37.bottom"),sQuery(id+"F4.wireOp",EDGE,"E37.left")])]})});
            var Q54;
            Q54=makeQuery(id+"F5.boolean.opBoolean","COPY",EDGE,{"derivedFrom":makeQuery(id+"F5.opExtrude","CAP_EDGE",EDGE,{"disambiguationData":[OSD([sQuery(id+"F4.wireOp",EDGE,"E36.left")])],"isStart":true})});
            var Q55;
            Q55=makeQuery(id+"F5.boolean.opBoolean","COPY",EDGE,{"derivedFrom":makeQuery(id+"F5.opExtrude","CAP_EDGE",EDGE,{"disambiguationData":[OSD([sQuery(id+"F4.wireOp",EDGE,"E35.left")])],"isStart":true})});
            var Q56;
            Q56=makeQuery(id+"F5.boolean.opBoolean","COPY",EDGE,{"derivedFrom":makeQuery(id+"F5.opExtrude","CAP_EDGE",EDGE,{"disambiguationData":[OSD([sQuery(id+"F4.wireOp",EDGE,"E34.left")])],"isStart":true})});
            var Q57;
            Q57=makeQuery(id+"F5.boolean.opBoolean","COPY",EDGE,{"derivedFrom":makeQuery(id+"F5.opExtrude","CAP_EDGE",EDGE,{"disambiguationData":[OSD([sQuery(id+"F4.wireOp",EDGE,"E33.left")])],"isStart":true})});
            var Q58;
            Q58=makeQuery(id+"F5.boolean.opBoolean","COPY",EDGE,{"derivedFrom":makeQuery(id+"F5.opExtrude","CAP_EDGE",EDGE,{"disambiguationData":[OSD([sQuery(id+"F4.wireOp",EDGE,"E32.left")])],"isStart":true})});
            var Q59;
            Q59=makeQuery(id+"F5.boolean.opBoolean","COPY",EDGE,{"derivedFrom":makeQuery(id+"F5.opExtrude","CAP_EDGE",EDGE,{"disambiguationData":[OSD([sQuery(id+"F4.wireOp",EDGE,"E37.left")])],"isStart":true})});
            fillet(context, id + "F6", {"entities" : qUnion([Q0, Q1, Q2, Q3, Q4, Q5, Q6, Q7, Q8, Q9, Q10, Q11, Q12, Q13, Q14, Q15, Q16, Q17, Q18, Q19, Q20, Q21, Q22, Q23, Q24, Q25, Q26, Q27, Q28, Q29, Q30, Q31, Q32, Q33, Q34, Q35, Q36, Q37, Q38, Q39, Q40, Q41, Q42, Q43, Q44, Q45, Q46, Q47, Q48, Q49, Q50, Q51, Q52, Q53, Q54, Q55, Q56, Q57, Q58, Q59]), "radius" : 1 * mm, "tangentPropagation" : true, "allowEdgeOverflow" : false});
        }
    });
